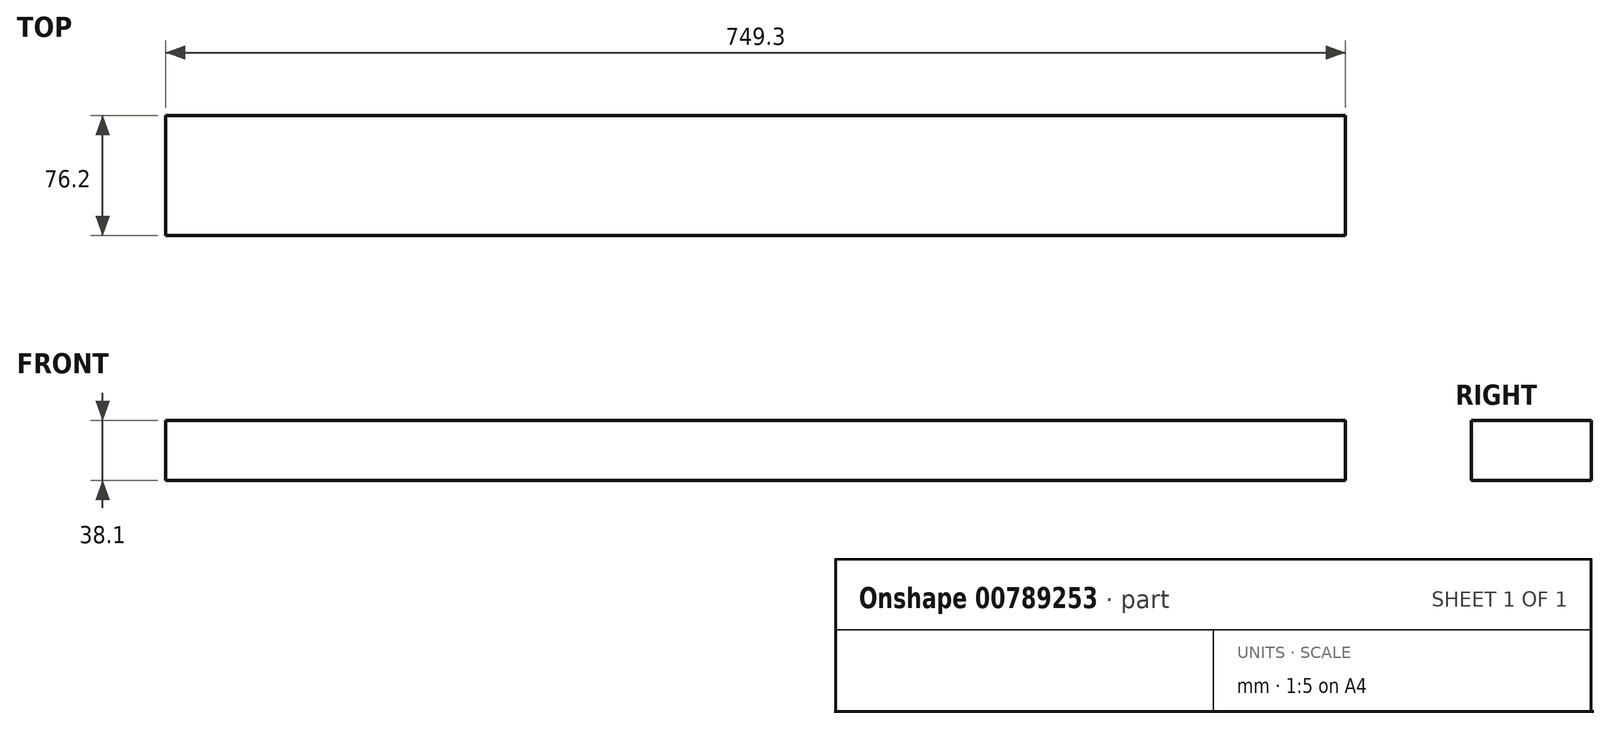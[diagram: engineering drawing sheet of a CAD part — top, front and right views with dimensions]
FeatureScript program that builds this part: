
annotation { "Feature Type Name" : "Feature", "Feature Type Description" : "" }
export const myFeature = defineFeature(function(context is Context, id is Id, definition is map)
    precondition{}
    {
        {
            var Q0;
            Q0=qCreatedBy(makeId("Front.planeOp"),FACE);
            var sketch = newSketch(context, id + "F0", { "sketchPlane" : qUnion([Q0])});
            skLineSegment(sketch, "E0.bottom", {"start": v(374.65, 19.05) * mm, "end": v(-374.65, 19.05) * mm});
            skLineSegment(sketch, "E0.top", {"start": v(374.65, -19.05) * mm, "end": v(-374.65, -19.05) * mm});
            skLineSegment(sketch, "E0.left", {"start": v(374.65, 19.05) * mm, "end": v(374.65, -19.05) * mm});
            skLineSegment(sketch, "E0.right", {"start": v(-374.65, 19.05) * mm, "end": v(-374.65, -19.05) * mm});
            skPoint(sketch, "E0.middle", {"position": v(0, 0) * mm});
            skSolve(sketch);
        }
        {
            var Q0;
            Q0 = qSketchRegion(id + "F0", true);
            extrude(context, id + "F1", {"entities" : qUnion([Q0]), "depth" : 76.2 * mm, "offsetDistance" : 25.4 * mm});
        }
    });
